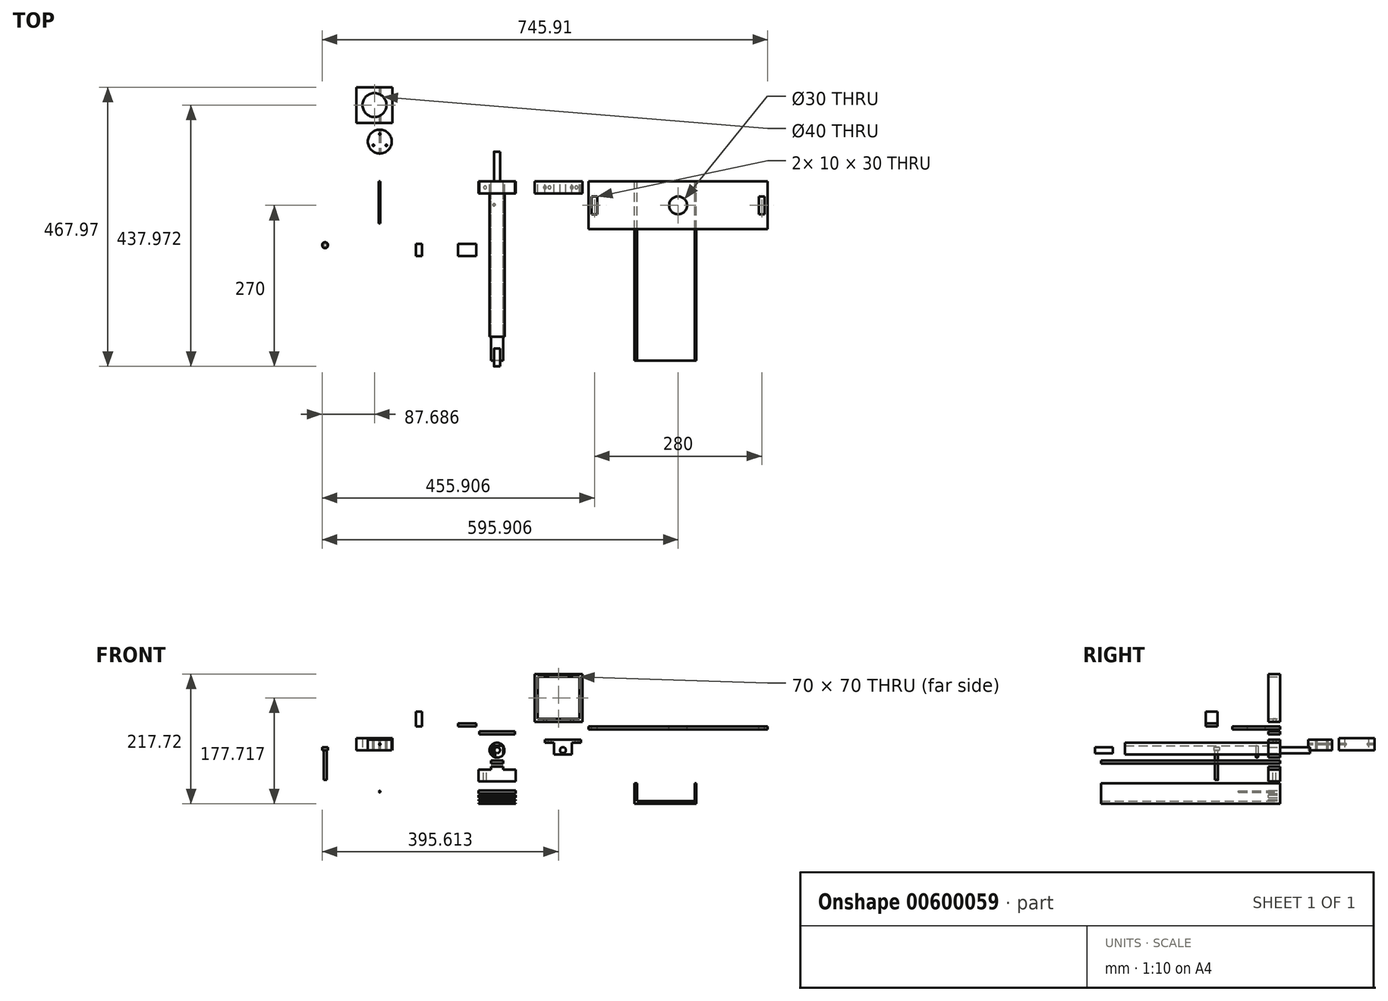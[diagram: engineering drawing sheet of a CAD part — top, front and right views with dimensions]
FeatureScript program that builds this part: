
annotation { "Feature Type Name" : "Feature", "Feature Type Description" : "" }
export const myFeature = defineFeature(function(context is Context, id is Id, definition is map)
    precondition{}
    {
        {
            var Q0;
            Q0=qCreatedBy(makeId("Front.planeOp"),FACE);
            var sketch = newSketch(context, id + "F0", { "sketchPlane" : qUnion([Q0])});
            skCircle(sketch, "E0", {"center": v(0, 0) * mm, "radius": 12.5 * mm});
            skCircle(sketch, "E1", {"center": v(110.3, 0) * mm, "radius": 5 * mm});
            skLineSegment(sketch, "E2.bottom", {"start": v(-30, 31.74) * mm, "end": v(30, 31.74) * mm});
            skLineSegment(sketch, "E2.top", {"start": v(-30, 26.74) * mm, "end": v(30, 26.74) * mm});
            skLineSegment(sketch, "E2.left", {"start": v(-30, 31.74) * mm, "end": v(-30, 26.74) * mm});
            skLineSegment(sketch, "E2.right", {"start": v(30, 31.74) * mm, "end": v(30, 26.74) * mm});
            skPoint(sketch, "E2.middle", {"position": v(0, 29.24) * mm});
            skLineSegment(sketch, "E3", {"start": v(110.3, 10) * mm, "end": v(110.3, -10) * mm, "construction": true});
            skCircle(sketch, "E4", {"center": v(110.3, 0) * mm, "radius": 12.5 * mm, "construction": true});
            skLineSegment(sketch, "E5", {"start": v(97.8, 0) * mm, "end": v(122.8, 0) * mm, "construction": true});
            skLineSegment(sketch, "E6", {"start": v(110.3, 12.5) * mm, "end": v(79.29, 12.5) * mm, "construction": true});
            skLineSegment(sketch, "E7", {"start": v(110.3, 5) * mm, "end": v(79.29, 5) * mm, "construction": true});
            skLineSegment(sketch, "E8", {"start": v(110.3, -5) * mm, "end": v(79.29, -5) * mm, "construction": true});
            skLineSegment(sketch, "E9", {"start": v(110.3, -12.5) * mm, "end": v(79.29, -12.5) * mm, "construction": true});
            skLineSegment(sketch, "E10", {"start": v(110.3, -7.5) * mm, "end": v(125.3, -7.5) * mm});
            skLineSegment(sketch, "E11", {"start": v(110.3, 17.5) * mm, "end": v(140.3, 17.5) * mm});
            skLineSegment(sketch, "E12", {"start": v(125.3, 12.5) * mm, "end": v(140.3, 12.5) * mm});
            skLineSegment(sketch, "E13", {"start": v(125.3, -7.5) * mm, "end": v(125.3, 12.5) * mm});
            skLineSegment(sketch, "E14", {"start": v(140.3, 17.5) * mm, "end": v(140.3, 12.5) * mm});
            skPoint(sketch, "E15.orphan", {"position": v(110.3, 12.5) * mm});
            skLineSegment(sketch, "E16.MirrorCS", {"start": v(95.3, 12.5) * mm, "end": v(80.3, 12.5) * mm});
            skLineSegment(sketch, "E17.MirrorCS", {"start": v(80.3, 17.5) * mm, "end": v(80.3, 12.5) * mm});
            skLineSegment(sketch, "E18.MirrorCS", {"start": v(110.3, 17.5) * mm, "end": v(80.3, 17.5) * mm});
            skLineSegment(sketch, "E19.MirrorCS", {"start": v(95.3, -7.5) * mm, "end": v(95.3, 12.5) * mm});
            skLineSegment(sketch, "E20.MirrorCS", {"start": v(110.3, -7.5) * mm, "end": v(95.3, -7.5) * mm});
            skLineSegment(sketch, "E21.top", {"start": v(0, -27.58) * mm, "end": v(10, -27.58) * mm});
            skLineSegment(sketch, "E22", {"start": v(10.93, -32.58) * mm, "end": v(30.93, -32.58) * mm});
            skLineSegment(sketch, "E23", {"start": v(30.93, -32.58) * mm, "end": v(30.93, -52.58) * mm});
            skLineSegment(sketch, "E24", {"start": v(30.93, -52.58) * mm, "end": v(0, -52.58) * mm});
            skLineSegment(sketch, "E25.MirrorCS", {"start": v(0, -27.58) * mm, "end": v(-10, -27.58) * mm});
            skLineSegment(sketch, "E26.MirrorCS", {"start": v(-10.93, -32.58) * mm, "end": v(-30.93, -32.58) * mm});
            skLineSegment(sketch, "E27.MirrorCS", {"start": v(-30.93, -32.58) * mm, "end": v(-30.93, -52.58) * mm});
            skLineSegment(sketch, "E28.MirrorCS", {"start": v(-30.93, -52.58) * mm, "end": v(0, -52.58) * mm});
            skLineSegment(sketch, "E29", {"start": v(0, -22.52) * mm, "end": v(10, -22.52) * mm});
            skLineSegment(sketch, "E30", {"start": v(10, -22.52) * mm, "end": v(10, -17.52) * mm});
            skLineSegment(sketch, "E31", {"start": v(10, -17.52) * mm, "end": v(0, -17.52) * mm});
            skLineSegment(sketch, "E32.MirrorCS", {"start": v(-10, -17.52) * mm, "end": v(0, -17.52) * mm});
            skLineSegment(sketch, "E33.MirrorCS", {"start": v(0, -22.52) * mm, "end": v(-10, -22.52) * mm});
            skLineSegment(sketch, "E34.MirrorCS", {"start": v(-10, -22.52) * mm, "end": v(-10, -17.52) * mm});
            skLineSegment(sketch, "E35.bottom", {"start": v(137.73, 52.7) * mm, "end": v(67.73, 52.7) * mm});
            skLineSegment(sketch, "E35.top", {"start": v(137.73, 122.7) * mm, "end": v(67.73, 122.7) * mm});
            skLineSegment(sketch, "E35.left", {"start": v(137.73, 52.7) * mm, "end": v(137.73, 122.7) * mm});
            skLineSegment(sketch, "E35.right", {"start": v(67.73, 52.7) * mm, "end": v(67.73, 122.7) * mm});
            skPoint(sketch, "E35.middle", {"position": v(102.73, 87.7) * mm});
            skLineSegment(sketch, "E36.bottom", {"start": v(62.73, 127.7) * mm, "end": v(142.73, 127.7) * mm});
            skLineSegment(sketch, "E36.top", {"start": v(62.73, 47.7) * mm, "end": v(142.73, 47.7) * mm});
            skLineSegment(sketch, "E36.left", {"start": v(62.73, 127.7) * mm, "end": v(62.73, 47.7) * mm});
            skLineSegment(sketch, "E36.right", {"start": v(142.73, 127.7) * mm, "end": v(142.73, 47.7) * mm});
            skLineSegment(sketch, "E37.bottom", {"start": v(-30.93, -79.86) * mm, "end": v(30.93, -79.86) * mm});
            skLineSegment(sketch, "E37.top", {"start": v(-30.93, -74.86) * mm, "end": v(30.93, -74.86) * mm});
            skLineSegment(sketch, "E37.left", {"start": v(-30.93, -79.86) * mm, "end": v(-30.93, -74.86) * mm});
            skLineSegment(sketch, "E37.right", {"start": v(30.93, -79.86) * mm, "end": v(30.93, -74.86) * mm});
            skLineSegment(sketch, "E38.MirrorCS", {"start": v(-30.74, -88.65) * mm, "end": v(31.12, -88.65) * mm});
            skLineSegment(sketch, "E39.MirrorCS", {"start": v(-30.74, -89.65) * mm, "end": v(31.12, -89.65) * mm});
            skLineSegment(sketch, "E40", {"start": v(-30.93, -82.76) * mm, "end": v(30.93, -82.76) * mm});
            skLineSegment(sketch, "E41", {"start": v(30.93, -82.76) * mm, "end": v(30.93, -84.76) * mm});
            skLineSegment(sketch, "E42", {"start": v(30.93, -84.76) * mm, "end": v(-30.93, -84.76) * mm});
            skLineSegment(sketch, "E43", {"start": v(-30.93, -84.76) * mm, "end": v(-30.93, -82.76) * mm});
            skLineSegment(sketch, "E44", {"start": v(-30.74, -88.65) * mm, "end": v(-30.74, -89.65) * mm});
            skLineSegment(sketch, "E45", {"start": v(31.12, -88.65) * mm, "end": v(31.12, -89.65) * mm});
            skLineSegment(sketch, "E46", {"start": v(-30.93, -72.74) * mm, "end": v(30.93, -72.74) * mm});
            skLineSegment(sketch, "E47", {"start": v(30.93, -72.74) * mm, "end": v(30.93, -67.74) * mm});
            skLineSegment(sketch, "E48", {"start": v(30.93, -67.74) * mm, "end": v(-30.93, -67.74) * mm});
            skLineSegment(sketch, "E49", {"start": v(-30.93, -67.74) * mm, "end": v(-30.93, -72.74) * mm});
            skLineSegment(sketch, "E50", {"start": v(-10, -27.58) * mm, "end": v(-10, -32.58) * mm});
            skLineSegment(sketch, "E51", {"start": v(-10, -32.58) * mm, "end": v(-10.93, -32.58) * mm});
            skPoint(sketch, "E52.MirrorCS.end.orphan", {"position": v(-10, -27.58) * mm});
            skPoint(sketch, "E52.MirrorCS.start.orphan", {"position": v(-10.93, -32.58) * mm});
            skLineSegment(sketch, "E53", {"start": v(10, -27.58) * mm, "end": v(10, -32.58) * mm});
            skLineSegment(sketch, "E54", {"start": v(10, -32.58) * mm, "end": v(10.93, -32.58) * mm});
            skLineSegment(sketch, "E55.left", {"start": v(194.47, 95.4) * mm, "end": v(194.47, 97.9) * mm});
            skLineSegment(sketch, "E56.bottom", {"start": v(-122.7, 157) * mm, "end": v(-422.7, 157) * mm});
            skLineSegment(sketch, "E56.top", {"start": v(-122.7, 159.5) * mm, "end": v(-422.7, 159.5) * mm});
            skLineSegment(sketch, "E56.left", {"start": v(-122.7, 157) * mm, "end": v(-122.7, 159.5) * mm});
            skLineSegment(sketch, "E56.right", {"start": v(-422.7, 157) * mm, "end": v(-422.7, 159.5) * mm});
            skLineSegment(sketch, "E57", {"start": v(-272.7, 150) * mm, "end": v(-272.7, 153.49) * mm, "construction": true});
            skPoint(sketch, "E57.startSnap0", {"position": v(-272.7, 157) * mm});
            skSolve(sketch);
        }
        {
            var Q0;
            Q0=makeQuery(id+"F0.imprint","IMPRINT",FACE,{"disambiguationData":[TD([[makeQuery(id+"F0.imprint","IMPRINT",EDGE,{"derivedFrom":sQuery(id+"F0.wireOp",EDGE,"E1")}),-1.0]])]});
            var Q1;
            Q1=makeQuery(id+"F0.imprint","IMPRINT",FACE,{"disambiguationData":[TD([[makeQuery(id+"F0.imprint","IMPRINT",EDGE,{"derivedFrom":sQuery(id+"F0.wireOp",EDGE,"E2.bottom")}),-1.0]])]});
            var Q2;
            Q2=makeQuery(id+"F0.imprint","IMPRINT",FACE,{"disambiguationData":[TD([[makeQuery(id+"F0.imprint","IMPRINT",EDGE,{"derivedFrom":sQuery(id+"F0.wireOp",EDGE,"E21.top")}),-1.0]])]});
            var Q3;
            Q3=makeQuery(id+"F0.imprint","IMPRINT",FACE,{"disambiguationData":[TD([[makeQuery(id+"F0.imprint","IMPRINT",EDGE,{"derivedFrom":sQuery(id+"F0.wireOp",EDGE,"E35.bottom")}),1.0]])]});
            var Q4;
            Q4=makeQuery(id+"F0.imprint","IMPRINT",FACE,{"disambiguationData":[TD([[makeQuery(id+"F0.imprint","IMPRINT",EDGE,{"derivedFrom":sQuery(id+"F0.wireOp",EDGE,"E37.bottom")}),1.0]])]});
            var Q5;
            Q5=makeQuery(id+"F0.imprint","IMPRINT",FACE,{"disambiguationData":[TD([[makeQuery(id+"F0.imprint","IMPRINT",EDGE,{"derivedFrom":sQuery(id+"F0.wireOp",EDGE,"E38.MirrorCS")}),-1.0]])]});
            var Q6;
            Q6=makeQuery(id+"F0.imprint","IMPRINT",FACE,{"disambiguationData":[TD([[makeQuery(id+"F0.imprint","IMPRINT",EDGE,{"derivedFrom":sQuery(id+"F0.wireOp",EDGE,"E40")}),-1.0]])]});
            var Q7;
            Q7=makeQuery(id+"F0.imprint","IMPRINT",FACE,{"disambiguationData":[TD([[makeQuery(id+"F0.imprint","IMPRINT",EDGE,{"derivedFrom":sQuery(id+"F0.wireOp",EDGE,"E46")}),1.0]])]});
            var Q8;
            {var subQ5=sQuery(id+"F0.wireOp",EDGE,"E55.right");Q8=makeQuery(id+"F0.imprint","IMPRINT",FACE,{"disambiguationData":[TD([[makeQuery(id+"F0.imprint","IMPRINT",EDGE,{"derivedFrom":subQ5}),-1.0]])]});}
            extrude(context, id + "F1", {"entities" : qUnion([Q0, Q1, Q2, Q3, Q4, Q5, Q6, Q7, Q8]), "depth" : 20 * mm, "offsetDistance" : 25 * mm});
        }
        {
            var Q0;
            Q0=makeQuery(id+"F0.imprint","IMPRINT",FACE,{"disambiguationData":[TD([[makeQuery(id+"F0.imprint","IMPRINT",EDGE,{"derivedFrom":sQuery(id+"F0.wireOp",EDGE,"E0")}),1.0]])]});
            extrude(context, id + "F2", {"entities" : qUnion([Q0]), "depth" : 260 * mm, "offsetDistance" : 25 * mm});
        }
        {
            var Q0;
            Q0=makeQuery(id+"F2.opExtrude","CAP_FACE",FACE,{"disambiguationData":[OSD([sQuery(id+"F0.wireOp",EDGE,"E0")])],"isStart":false});
            var sketch = newSketch(context, id + "F3", { "sketchPlane" : qUnion([Q0])});
            skCircle(sketch, "E58", {"center": v(0, 0) * mm, "radius": 5 * mm});
            skSolve(sketch);
        }
        {
            var Q0;
            Q0=makeQuery(id+"F3.imprint","IMPRINT",FACE,{"disambiguationData":[TD([[makeQuery(id+"F3.imprint","IMPRINT",EDGE,{"derivedFrom":sQuery(id+"F3.wireOp",EDGE,"E58")}),1.0]])]});
            extrude(context, id + "F4", {"entities" : qUnion([Q0]), "operationType" : NewBodyOperationType.ADD, "depth" : 50 * mm, "offsetDistance" : 25 * mm});
        }
        {
            var Q0;
            Q0=makeQuery(id+"F0.imprint","IMPRINT",FACE,{"disambiguationData":[TD([[makeQuery(id+"F0.imprint","IMPRINT",EDGE,{"derivedFrom":sQuery(id+"F0.wireOp",EDGE,"E29")}),1.0]])]});
            extrude(context, id + "F5", {"entities" : qUnion([Q0]), "depth" : 300 * mm, "offsetDistance" : 25 * mm});
        }
        {
            var Q0;
            Q0=makeQuery(id+"F1.opExtrude","SWEPT_FACE",FACE,{"disambiguationData":[OSD([sQuery(id+"F0.wireOp",EDGE,"E26.MirrorCS")])]});
            var sketch = newSketch(context, id + "F6", { "sketchPlane" : qUnion([Q0])});
            skCircle(sketch, "E59", {"center": v(-20, -10) * mm, "radius": 2.5 * mm});
            skSolve(sketch);
        }
        {
            var Q0;
            Q0=makeQuery(id+"F6.imprint","IMPRINT",FACE,{"disambiguationData":[TD([[makeQuery(id+"F6.imprint","IMPRINT",EDGE,{"derivedFrom":sQuery(id+"F6.wireOp",EDGE,"E59")}),1.0]])]});
            var Q1;
            Q1=makeQuery(id+"FNYWGUJzlf6PVvf_4.imprint","IMPRINT",FACE,{"disambiguationData":[TD([[makeQuery(id+"FNYWGUJzlf6PVvf_4.imprint","IMPRINT",EDGE,{"derivedFrom":sQuery(id+"FNYWGUJzlf6PVvf_4.wireOp",EDGE,"JrdPBHnR-5tIZ-cZ5f-IPz8-CMVoVNEgzM20")}),1.0]])]});
            extrude(context, id + "F7", {"entities" : qUnion([Q0, Q1]), "operationType" : NewBodyOperationType.REMOVE, "oppositeDirection" : true, "depth" : 25 * mm, "offsetDistance" : 25 * mm});
        }
        {
            var Q0;
            Q0=makeQuery(id+"F1.opExtrude","SWEPT_FACE",FACE,{"disambiguationData":[OSD([sQuery(id+"F0.wireOp",EDGE,"E12")])]});
            var sketch = newSketch(context, id + "F8", { "sketchPlane" : qUnion([Q0])});
            skCircle(sketch, "E60", {"center": v(132.8, 10) * mm, "radius": 2.5 * mm});
            skPoint(sketch, "E60.centerSnap0", {"position": v(132.8, 20) * mm});
            skPoint(sketch, "E60.centerSnap1", {"position": v(125.3, 10) * mm});
            skSolve(sketch);
        }
        {
            var Q0;
            Q0=makeQuery(id+"F1.opExtrude","SWEPT_FACE",FACE,{"disambiguationData":[OSD([sQuery(id+"F0.wireOp",EDGE,"E16.MirrorCS")])]});
            var sketch = newSketch(context, id + "F9", { "sketchPlane" : qUnion([Q0])});
            skCircle(sketch, "E61", {"center": v(87.8, 10) * mm, "radius": 2.5 * mm});
            skPoint(sketch, "E61.centerSnap0", {"position": v(80.3, 10) * mm});
            skPoint(sketch, "E61.centerSnap1", {"position": v(87.8, 20) * mm});
            skSolve(sketch);
        }
        {
            var Q0;
            Q0=makeQuery(id+"F9.imprint","IMPRINT",FACE,{"disambiguationData":[TD([[makeQuery(id+"F9.imprint","IMPRINT",EDGE,{"derivedFrom":sQuery(id+"F9.wireOp",EDGE,"E61")}),1.0]])]});
            var Q1;
            Q1=makeQuery(id+"F8.imprint","IMPRINT",FACE,{"disambiguationData":[TD([[makeQuery(id+"F8.imprint","IMPRINT",EDGE,{"derivedFrom":sQuery(id+"F8.wireOp",EDGE,"E60")}),1.0]])]});
            extrude(context, id + "F10", {"entities" : qUnion([Q0, Q1]), "operationType" : NewBodyOperationType.REMOVE, "oppositeDirection" : true, "depth" : 25 * mm, "offsetDistance" : 25 * mm});
        }
        {
            var Q0;
            Q0=makeQuery(id+"F5.opExtrude","SWEPT_FACE",FACE,{"disambiguationData":[OSD([sQuery(id+"F0.wireOp",EDGE,"E31"),sQuery(id+"F0.wireOp",EDGE,"E32.MirrorCS")])]});
            var sketch = newSketch(context, id + "F11", { "sketchPlane" : qUnion([Q0])});
            skLineSegment(sketch, "E62", {"start": v(-10, -280) * mm, "end": v(10, -280) * mm});
            skCircle(sketch, "E63", {"center": v(5, -39.13) * mm, "radius": 1.93 * mm});
            skPoint(sketch, "E64.orphan", {"position": v(0, -300) * mm});
            skCircle(sketch, "E65.MirrorC", {"center": v(-5, -39.13) * mm, "radius": 1.93 * mm});
            skLineSegment(sketch, "E66", {"start": v(10, -20) * mm, "end": v(-10, -20) * mm});
            skSolve(sketch);
        }
        {
            var Q0;
            Q0=makeQuery(id+"F11.imprint","IMPRINT",FACE,{"disambiguationData":[TD([[makeQuery(id+"F11.imprint","IMPRINT",EDGE,{"derivedFrom":sQuery(id+"F11.wireOp",EDGE,"E65.MirrorC")}),-1.0]])]});
            var Q1;
            Q1=makeQuery(id+"F11.imprint","IMPRINT",FACE,{"disambiguationData":[TD([[makeQuery(id+"F11.imprint","IMPRINT",EDGE,{"derivedFrom":sQuery(id+"F11.wireOp",EDGE,"E63")}),1.0]])]});
            extrude(context, id + "F12", {"entities" : qUnion([Q0, Q1]), "operationType" : NewBodyOperationType.REMOVE, "depth" : 25 * mm, "offsetDistance" : 25 * mm});
        }
        {
            var Q0;
            Q0=makeQuery(id+"F1.opExtrude","SWEPT_FACE",FACE,{"disambiguationData":[OSD([sQuery(id+"F0.wireOp",EDGE,"E36.top")])]});
            var sketch = newSketch(context, id + "F13", { "sketchPlane" : qUnion([Q0])});
            skCircle(sketch, "E67", {"center": v(80.23, 10) * mm, "radius": 2.5 * mm});
            skCircle(sketch, "E68", {"center": v(125.23, 10) * mm, "radius": 2.5 * mm});
            skLineSegment(sketch, "E69", {"start": v(62.73, 20) * mm, "end": v(142.73, 20) * mm, "construction": true});
            skLineSegment(sketch, "E70", {"start": v(142.73, 20) * mm, "end": v(142.73, 0) * mm, "construction": true});
            skLineSegment(sketch, "E71", {"start": v(142.73, 0) * mm, "end": v(62.73, 0) * mm, "construction": true});
            skLineSegment(sketch, "E72", {"start": v(62.73, 0) * mm, "end": v(62.73, 20) * mm, "construction": true});
            skLineSegment(sketch, "E73", {"start": v(67.73, 20) * mm, "end": v(67.73, 0) * mm, "construction": true});
            skLineSegment(sketch, "E74", {"start": v(137.73, 20) * mm, "end": v(137.73, 0) * mm, "construction": true});
            skSolve(sketch);
        }
        {
            var Q0;
            Q0=makeQuery(id+"F2.opExtrude","CAP_FACE",FACE,{"disambiguationData":[OSD([sQuery(id+"F0.wireOp",EDGE,"E0")])],"isStart":true});
            var sketch = newSketch(context, id + "F14", { "sketchPlane" : qUnion([Q0])});
            skCircle(sketch, "E75", {"center": v(0, 0) * mm, "radius": 5 * mm});
            skSolve(sketch);
        }
        {
            var Q0;
            Q0=qSketchRegion(id+"F14",true);
            extrude(context, id + "F15", {"entities" : qUnion([Q0]), "operationType" : NewBodyOperationType.ADD, "depth" : 50 * mm, "offsetDistance" : 25 * mm});
        }
        {
            var Q0;
            Q0=qCreatedBy(makeId("Front.planeOp"),FACE);
            var sketch = newSketch(context, id + "F16", { "sketchPlane" : qUnion([Q0])});
            skLineSegment(sketch, "E76.bottom", {"start": v(153.03, 39.78) * mm, "end": v(453.03, 39.78) * mm});
            skLineSegment(sketch, "E76.top", {"start": v(153.03, 34.78) * mm, "end": v(453.03, 34.78) * mm});
            skLineSegment(sketch, "E76.left", {"start": v(153.03, 39.78) * mm, "end": v(153.03, 34.78) * mm});
            skLineSegment(sketch, "E76.right", {"start": v(453.03, 39.78) * mm, "end": v(453.03, 34.78) * mm});
            skSolve(sketch);
        }
        {
            var Q0;
            Q0=makeQuery(id+"F16.imprint","IMPRINT",FACE,{"disambiguationData":[TD([[makeQuery(id+"F16.imprint","IMPRINT",EDGE,{"derivedFrom":sQuery(id+"F16.wireOp",EDGE,"E76.bottom")}),-1.0]])]});
            extrude(context, id + "F17", {"entities" : qUnion([Q0]), "depth" : 80 * mm, "offsetDistance" : 25 * mm});
        }
        {
            var Q0;
            Q0=makeQuery(id+"F17.opExtrude","SWEPT_FACE",FACE,{"disambiguationData":[OSD([sQuery(id+"F16.wireOp",EDGE,"E76.bottom")])]});
            var sketch = newSketch(context, id + "F18", { "sketchPlane" : qUnion([Q0])});
            skLineSegment(sketch, "E77", {"start": v(173.03, 0) * mm, "end": v(173.03, -80) * mm});
            skLineSegment(sketch, "E78.bottom", {"start": v(158.03, -25) * mm, "end": v(168.03, -25) * mm});
            skLineSegment(sketch, "E78.top", {"start": v(158.03, -55) * mm, "end": v(168.03, -55) * mm});
            skLineSegment(sketch, "E78.left", {"start": v(158.03, -25) * mm, "end": v(158.03, -55) * mm});
            skLineSegment(sketch, "E78.right", {"start": v(168.03, -25) * mm, "end": v(168.03, -55) * mm});
            skPoint(sketch, "E78.middle", {"position": v(163.03, -40) * mm});
            skLineSegment(sketch, "E79", {"start": v(303.03, 0) * mm, "end": v(303.03, -80) * mm, "construction": true});
            skLineSegment(sketch, "E80.MirrorCS", {"start": v(438.03, -25) * mm, "end": v(438.03, -55) * mm});
            skLineSegment(sketch, "E81.MirrorCS", {"start": v(448.03, -25) * mm, "end": v(438.03, -25) * mm});
            skLineSegment(sketch, "E82.MirrorCS", {"start": v(448.03, -25) * mm, "end": v(448.03, -55) * mm});
            skLineSegment(sketch, "E83.MirrorCS", {"start": v(448.03, -55) * mm, "end": v(438.03, -55) * mm});
            skLineSegment(sketch, "E84.MirrorCS", {"start": v(433.03, 0) * mm, "end": v(433.03, -80) * mm});
            skLineSegment(sketch, "E85.bottom", {"start": v(-65.07, -104.85) * mm, "end": v(-35.07, -104.85) * mm});
            skLineSegment(sketch, "E85.top", {"start": v(-65.07, -124.85) * mm, "end": v(-35.07, -124.85) * mm});
            skLineSegment(sketch, "E85.left", {"start": v(-65.07, -104.85) * mm, "end": v(-65.07, -124.85) * mm});
            skLineSegment(sketch, "E85.right", {"start": v(-35.07, -104.85) * mm, "end": v(-35.07, -124.85) * mm});
            skLineSegment(sketch, "E86.bottom", {"start": v(-135.53, -104.85) * mm, "end": v(-125.53, -104.85) * mm});
            skLineSegment(sketch, "E86.top", {"start": v(-135.53, -124.85) * mm, "end": v(-125.53, -124.85) * mm});
            skLineSegment(sketch, "E86.left", {"start": v(-135.53, -104.85) * mm, "end": v(-135.53, -124.85) * mm});
            skLineSegment(sketch, "E86.right", {"start": v(-125.53, -104.85) * mm, "end": v(-125.53, -124.85) * mm});
            skCircle(sketch, "E87", {"center": v(303.03, -40) * mm, "radius": 15 * mm});
            skSolve(sketch);
        }
        {
            var Q0;
            Q0=qCreatedBy(makeId("Top.planeOp"),FACE);
            var sketch = newSketch(context, id + "F19", { "sketchPlane" : qUnion([Q0])});
            skCircle(sketch, "E88", {"center": v(-196.27, 66.8) * mm, "radius": 20 * mm});
            skLineSegment(sketch, "E89.bottom", {"start": v(-235.2, 97.97) * mm, "end": v(-175.2, 97.97) * mm});
            skLineSegment(sketch, "E89.top", {"start": v(-235.2, 157.97) * mm, "end": v(-175.2, 157.97) * mm});
            skLineSegment(sketch, "E89.left", {"start": v(-235.2, 97.97) * mm, "end": v(-235.2, 157.97) * mm});
            skLineSegment(sketch, "E89.right", {"start": v(-175.2, 97.97) * mm, "end": v(-175.2, 157.97) * mm});
            skCircle(sketch, "E90", {"center": v(-205.2, 127.97) * mm, "radius": 20 * mm});
            skPoint(sketch, "E90.centerSnap0", {"position": v(-175.2, 127.97) * mm});
            skPoint(sketch, "E90.centerSnap1", {"position": v(-205.2, 97.97) * mm});
            skLineSegment(sketch, "E91", {"start": v(-196.27, 46.8) * mm, "end": v(-222.09, 46.8) * mm});
            skSolve(sketch);
        }
        {
            var Q0;
            Q0=makeQuery(id+"F19.imprint","IMPRINT",FACE,{"disambiguationData":[TD([[makeQuery(id+"F19.imprint","IMPRINT",EDGE,{"derivedFrom":sQuery(id+"F19.wireOp",EDGE,"E88")}),1.0]])]});
            extrude(context, id + "F20", {"entities" : qUnion([Q0]), "depth" : 17.5 * mm, "offsetDistance" : 25 * mm});
        }
        {
            var Q0;
            Q0=makeQuery(id+"F19.imprint","IMPRINT",FACE,{"disambiguationData":[TD([[makeQuery(id+"F19.imprint","IMPRINT",EDGE,{"derivedFrom":sQuery(id+"F19.wireOp",EDGE,"E89.bottom")}),1.0]])]});
            extrude(context, id + "F21", {"entities" : qUnion([Q0]), "depth" : 20 * mm, "offsetDistance" : 25 * mm});
        }
        {
            var Q0;
            Q0=makeQuery(id+"F18.imprint","IMPRINT",FACE,{"disambiguationData":[TD([[makeQuery(id+"F18.imprint","IMPRINT",EDGE,{"derivedFrom":sQuery(id+"F18.wireOp",EDGE,"E78.bottom")}),-1.0]])]});
            var Q1;
            Q1=makeQuery(id+"F18.imprint","IMPRINT",FACE,{"disambiguationData":[TD([[makeQuery(id+"F18.imprint","IMPRINT",EDGE,{"derivedFrom":sQuery(id+"F18.wireOp",EDGE,"E80.MirrorCS")}),1.0]])]});
            var Q2;
            Q2=makeQuery(id+"F18.imprint","IMPRINT",FACE,{"disambiguationData":[TD([[makeQuery(id+"F18.imprint","IMPRINT",EDGE,{"derivedFrom":sQuery(id+"F18.wireOp",EDGE,"E87")}),1.0]])]});
            extrude(context, id + "F22", {"entities" : qUnion([Q0, Q1, Q2]), "operationType" : NewBodyOperationType.REMOVE, "endBound" : BoundingType.THROUGH_ALL, "oppositeDirection" : true, "depth" : 25 * mm, "offsetDistance" : 25 * mm});
        }
        {
            var Q0;
            Q0=makeQuery(id+"F18.imprint","IMPRINT",FACE,{"disambiguationData":[TD([[makeQuery(id+"F18.imprint","IMPRINT",EDGE,{"derivedFrom":sQuery(id+"F18.wireOp",EDGE,"E86.bottom")}),-1.0]])]});
            extrude(context, id + "F23", {"entities" : qUnion([Q0]), "depth" : 25 * mm, "offsetDistance" : 25 * mm});
        }
        {
            var Q0;
            Q0=makeQuery(id+"F18.imprint","IMPRINT",FACE,{"disambiguationData":[TD([[makeQuery(id+"F18.imprint","IMPRINT",EDGE,{"derivedFrom":sQuery(id+"F18.wireOp",EDGE,"E85.bottom")}),-1.0]])]});
            extrude(context, id + "F24", {"entities" : qUnion([Q0]), "depth" : 5 * mm, "offsetDistance" : 25 * mm});
        }
        {
            var Q0;
            Q0=makeQuery(id+"F13.imprint","IMPRINT",FACE,{"disambiguationData":[TD([[makeQuery(id+"F13.imprint","IMPRINT",EDGE,{"derivedFrom":sQuery(id+"F13.wireOp",EDGE,"E68")}),1.0]])]});
            var Q1;
            Q1=makeQuery(id+"F13.imprint","IMPRINT",FACE,{"disambiguationData":[TD([[makeQuery(id+"F13.imprint","IMPRINT",EDGE,{"derivedFrom":sQuery(id+"F13.wireOp",EDGE,"E67")}),1.0]])]});
            extrude(context, id + "F25", {"entities" : qUnion([Q0, Q1]), "operationType" : NewBodyOperationType.REMOVE, "endBound" : BoundingType.UP_TO_NEXT, "oppositeDirection" : true, "depth" : 25 * mm, "offsetDistance" : 25 * mm});
        }
        {
            var Q0;
            Q0=qCreatedBy(makeId("Top.planeOp"),FACE);
            var sketch = newSketch(context, id + "F26", { "sketchPlane" : qUnion([Q0])});
            skCircle(sketch, "E92", {"center": v(-287.88, -106.71) * mm, "radius": 5 * mm});
            skSolve(sketch);
        }
        {
            var Q0;
            Q0=makeQuery(id+"F26.imprint","IMPRINT",FACE,{"disambiguationData":[TD([[makeQuery(id+"F26.imprint","IMPRINT",EDGE,{"derivedFrom":sQuery(id+"F26.wireOp",EDGE,"E92")}),1.0]])]});
            extrude(context, id + "F27", {"entities" : qUnion([Q0]), "depth" : 5 * mm, "offsetDistance" : 25 * mm});
        }
        {
            var Q0;
            Q0=makeQuery(id+"F26.imprint","IMPRINT",FACE,{"disambiguationData":[TD([[makeQuery(id+"F26.imprint","IMPRINT",EDGE,{"derivedFrom":sQuery(id+"F26.wireOp",EDGE,"E92")}),1.0]])]});
            var sketch = newSketch(context, id + "F28", { "sketchPlane" : qUnion([Q0])});
            skCircle(sketch, "E93", {"center": v(-287.73, -106.85) * mm, "radius": 2.5 * mm});
            skSolve(sketch);
        }
        {
            var Q0;
            Q0=makeQuery(id+"F28.imprint","IMPRINT",FACE,{"disambiguationData":[TD([[makeQuery(id+"F28.imprint","IMPRINT",EDGE,{"derivedFrom":sQuery(id+"F28.wireOp",EDGE,"E93")}),1.0]])]});
            extrude(context, id + "F29", {"entities" : qUnion([Q0]), "operationType" : NewBodyOperationType.ADD, "oppositeDirection" : true, "depth" : 50 * mm, "offsetDistance" : 25 * mm});
        }
        {
            var Q0;
            Q0=sQuery(id+"F19.wireOp",EDGE,"E91");
            extrude(context, id + "F30", {"bodyType" : ToolBodyType.SURFACE, "surfaceEntities" : qUnion([Q0]), "depth" : 20 * mm, "offsetDistance" : 25 * mm});
        }
        {
            var Q0;
            Q0=makeQuery(id+"F30.opExtrude","SWEPT_FACE",FACE,{"disambiguationData":[OSD([sQuery(id+"F19.wireOp",EDGE,"E91")])]});
            var sketch = newSketch(context, id + "F31", { "sketchPlane" : qUnion([Q0])});
            skCircle(sketch, "E94", {"center": v(196.27, 10) * mm, "radius": 1.25 * mm});
            skSolve(sketch);
        }
        {
            var Q0;
            {var subQ0=sQuery(id+"F31.wireOp",EDGE,"E94");var subQ1=makeQuery(id+"F30.opExtrude","SWEPT_EDGE",EDGE,{"disambiguationData":[OSD([sQuery(id+"F19.wireOp",VERTEX,"E91.start")])]});var subQ2=makeQuery(id+"F31.imprint","INTERSECT",VERTEX,{"disambiguationData":[OD(0.0)],"derivedFrom":[subQ1,subQ0]});Q0=makeQuery(id+"F31.imprint","IMPRINT",FACE,{"disambiguationData":[TD([[makeQuery(id+"F31.imprint","IMPRINT",EDGE,{"disambiguationData":[TD([[subQ2,-1.0]])],"derivedFrom":subQ0}),1.0]])]});}
            var Q1;
            {var subQ0=sQuery(id+"F31.wireOp",EDGE,"E94");var subQ1=makeQuery(id+"F30.opExtrude","SWEPT_EDGE",EDGE,{"disambiguationData":[OSD([sQuery(id+"F19.wireOp",VERTEX,"E91.start")])]});var subQ2=makeQuery(id+"F31.imprint","INTERSECT",VERTEX,{"disambiguationData":[OD(0.0)],"derivedFrom":[subQ1,subQ0]});Q1=makeQuery(id+"F31.imprint","IMPRINT",FACE,{"disambiguationData":[TD([[makeQuery(id+"F31.imprint","IMPRINT",EDGE,{"disambiguationData":[TD([[subQ2,1.0]])],"derivedFrom":subQ0}),1.0]])]});}
            extrude(context, id + "F32", {"entities" : qUnion([Q0, Q1]), "operationType" : NewBodyOperationType.REMOVE, "endBound" : BoundingType.THROUGH_ALL, "depth" : 25 * mm, "offsetDistance" : 25 * mm});
        }
        {
            var Q0;
            Q0=qCreatedBy(makeId("Front.planeOp"),FACE);
            var sketch = newSketch(context, id + "F33", { "sketchPlane" : qUnion([Q0])});
            skCircle(sketch, "E95", {"center": v(-196.47, -69.5) * mm, "radius": 1.25 * mm});
            skSolve(sketch);
        }
        {
            var Q0;
            Q0=makeQuery(id+"F33.imprint","IMPRINT",FACE,{"disambiguationData":[TD([[makeQuery(id+"F33.imprint","IMPRINT",EDGE,{"derivedFrom":sQuery(id+"F33.wireOp",EDGE,"E95")}),1.0]])]});
            extrude(context, id + "F34", {"entities" : qUnion([Q0]), "depth" : 70 * mm, "offsetDistance" : 25 * mm});
        }
        {
            var Q0;
            Q0=makeQuery(id+"F20.opExtrude","CAP_FACE",FACE,{"disambiguationData":[OSD([sQuery(id+"F19.wireOp",EDGE,"E88")])],"isStart":false});
            var sketch = newSketch(context, id + "F35", { "sketchPlane" : qUnion([Q0])});
            skCircle(sketch, "E96", {"center": v(-196.27, 79.3) * mm, "radius": 1.25 * mm});
            skCircle(sketch, "E97", {"center": v(-185.44, 60.55) * mm, "radius": 1.25 * mm});
            skCircle(sketch, "E98", {"center": v(-207.1, 60.55) * mm, "radius": 1.25 * mm});
            skCircle(sketch, "E99", {"center": v(-196.27, 66.8) * mm, "radius": 12.5 * mm, "construction": true});
            skSolve(sketch);
        }
        {
            var Q0;
            Q0=makeQuery(id+"F35.imprint","IMPRINT",FACE,{"disambiguationData":[TD([[makeQuery(id+"F35.imprint","IMPRINT",EDGE,{"derivedFrom":sQuery(id+"F35.wireOp",EDGE,"E96")}),1.0]])]});
            var Q1;
            Q1=makeQuery(id+"F35.imprint","IMPRINT",FACE,{"disambiguationData":[TD([[makeQuery(id+"F35.imprint","IMPRINT",EDGE,{"derivedFrom":sQuery(id+"F35.wireOp",EDGE,"E97")}),1.0]])]});
            var Q2;
            Q2=makeQuery(id+"F35.imprint","IMPRINT",FACE,{"disambiguationData":[TD([[makeQuery(id+"F35.imprint","IMPRINT",EDGE,{"derivedFrom":sQuery(id+"F35.wireOp",EDGE,"E98")}),1.0]])]});
            extrude(context, id + "F36", {"entities" : qUnion([Q0, Q1, Q2]), "operationType" : NewBodyOperationType.REMOVE, "endBound" : BoundingType.THROUGH_ALL, "oppositeDirection" : true, "depth" : 25 * mm, "offsetDistance" : 25 * mm});
        }
        {
            var Q0;
            Q0=qCreatedBy(makeId("Front.planeOp"),FACE);
            var sketch = newSketch(context, id + "F37", { "sketchPlane" : qUnion([Q0])});
            skLineSegment(sketch, "E100.bottom", {"start": v(234.66, -85.01) * mm, "end": v(330.99, -85.01) * mm});
            skLineSegment(sketch, "E100.top", {"start": v(230.14, -90.01) * mm, "end": v(333.22, -90.01) * mm});
            skLineSegment(sketch, "E100.left", {"start": v(230.14, -85.01) * mm, "end": v(230.14, -90.01) * mm});
            skLineSegment(sketch, "E100.right", {"start": v(333.22, -85.01) * mm, "end": v(333.22, -90.01) * mm});
            skLineSegment(sketch, "E101", {"start": v(230.14, -85.01) * mm, "end": v(230.14, -55.71) * mm});
            skLineSegment(sketch, "E102", {"start": v(230.14, -55.71) * mm, "end": v(234.66, -55.71) * mm});
            skLineSegment(sketch, "E103", {"start": v(234.66, -55.71) * mm, "end": v(234.66, -85.01) * mm});
            skLineSegment(sketch, "E104", {"start": v(333.22, -85.01) * mm, "end": v(333.22, -55.71) * mm});
            skLineSegment(sketch, "E105", {"start": v(333.22, -55.71) * mm, "end": v(330.99, -55.71) * mm});
            skLineSegment(sketch, "E106", {"start": v(330.99, -55.71) * mm, "end": v(330.99, -85.01) * mm});
            skSolve(sketch);
        }
        {
            var Q0;
            Q0=makeQuery(id+"F37.imprint","IMPRINT",FACE,{"disambiguationData":[TD([[makeQuery(id+"F37.imprint","IMPRINT",EDGE,{"derivedFrom":sQuery(id+"F37.wireOp",EDGE,"E100.bottom")}),-1.0]])]});
            extrude(context, id + "F38", {"entities" : qUnion([Q0]), "depth" : 300 * mm, "offsetDistance" : 25 * mm});
        }
    });
